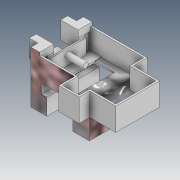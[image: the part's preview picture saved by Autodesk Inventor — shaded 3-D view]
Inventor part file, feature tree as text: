
AUTODESK INVENTOR PART (.ipt)
format: ipt  version: 2021 (Build 250183000, 183)  size: 703,488 bytes
history: native  units: in
note: dims shown in document units (in); Inventor stores cm internally (conversion verified against a paired STEP export)
features: extrude x36, sketch x36, other x1
ambient origin geometry x8: Origin, YZ Plane, XZ Plane, XY Plane, X Axis, Y Axis, Z Axis, Center Point
bodies: Body1 (feature_tree), Body2 (feature_tree)
feature tree (73):
  other  "Sólido1"
  extrude  "Extrusão1"  Depth=0.1969in
  extrude  "Extrusão2"  Depth=0.3937in
  extrude  "Extrusão3"  Depth=0.0984in
  extrude  "Extrusão4"  Depth=0.1969in
  extrude  "Extrusão5"  Depth=0.3937in
  extrude  "Extrusão6"  Depth=0.0079in
  extrude  "Extrusão7"  Depth=0.0079in
  extrude  "Extrusão10"  Depth=0.0079in
  extrude  "Extrusão11"  Depth=0.0079in
  extrude  "Extrusão12"  Depth=0.0079in
  extrude  "Extrusão13"  Depth=0.0079in
  extrude  "Extrusão16"  Depth=0.0079in
  extrude  "Extrusão20"  Depth=0.0079in
  extrude  "Extrusão25"  Depth=0.1575in
  extrude  "Extrusão26"  Depth=0.0079in
  extrude  "Extrusão27"  Depth=0.0394in
  extrude  "Extrusão28"  Depth=0.0787in
  extrude  "Extrusão29"  Depth=1.1811in TaperAngle=0.0deg
  extrude  "Extrusão30"  Depth=0.3543in
  extrude  "Extrusão31"  Depth=0.1181in
  extrude  "Extrusão32"  Depth=0.1969in TaperAngle=0.0deg
  extrude  "Extrusão33"  Depth=0.0591in
  extrude  "Extrusão34"  Depth=0.2559in
  extrude  "Extrusão35"  Depth=0.0315in TaperAngle=0.0deg
  extrude  "Extrusão36"  Depth=0.0394in
  extrude  "Extrusão37"  Depth=0.0394in
  extrude  "Extrusão38"  Depth=0.0394in
  extrude  "Extrusão39"  Depth=0.0394in
  extrude  "Extrusão40"  Depth=0.0394in TaperAngle=0.0deg
  extrude  "Extrusão41"  Depth=0.0197in TaperAngle=0.0deg
  extrude  "Extrusão42"  Depth=0.0197in TaperAngle=0.0deg
  extrude  "Extrusão43"  Depth=0.1969in
  extrude  "Extrusão44"  Depth=0.1181in
  extrude  "Extrusão45"  Depth=0.1969in
  extrude  "Extrusão46"  Depth=0.1181in
  extrude  "Extrusão47"  Depth=0.0039in
  sketch  "Esboço2"  dims[d0=0.1969in d1=0.1969in]
  sketch  "Esboço4"  dims[d2=0.1181in d3=0.3937in]
  sketch  "Esboço5"  dims[d4=0.1969in d5=0.0984in]
  sketch  "Esboço6"  dims[d6=0.3937in d7=0.1969in]
  sketch  "Esboço7"  dims[d8=0.1969in d9=0.3937in]
  sketch  "Esboço8"  dims[d11=0.1969in d12=0.0079in]
  sketch  "Esboço10"  dims[d13=0.0079in d14=0.0079in]
  sketch  "Esboço15"  dims[d15=0.0079in d16=0.0079in]
  sketch  "Esboço16"  dims[d17=0.0079in d19=0.0079in]
  sketch  "Esboço18"  dims[d20=0.0079in d21=0.0079in]
  sketch  "Esboço20"  dims[d22=0.0079in d23=0.0079in]
  sketch  "Esboço23"  dims[d24=0.0079in d25=0.0079in]
  sketch  "Esboço29"  dims[d26=0.0079in d27=0.0079in]
  sketch  "Esboço38"  dims[d28=0.2756in d29=0.1575in]
  sketch  "Esboço39"  dims[d30=0.2756in d31=0.0079in]
  sketch  "Esboço40"  dims[d32=0.0787in d33=0.0394in]
  sketch  "Esboço41"  dims[d34=0.0079in d35=0.0787in]
  sketch  "Esboço42"  dims[d36=0.0394in d37=1.1811in d38=0.0in]
  sketch  "Esboço43"  dims[d39=0.4724in d40=0.3543in]
  sketch  "Esboço44"  dims[d46=0.1969in d47=0.0in d48=0.1181in]
  sketch  "Esboço45"  dims[d49=0.5394in d50=0.0in d51=0.1969in d52=0.0in]
  sketch  "Esboço46"  dims[d53=0.1969in d54=0.0in d55=0.0591in]
  sketch  "Esboço47"  dims[d56=0.1969in d57=0.0in d58=0.2559in]
  sketch  "Esboço48"  dims[d59=0.2559in d60=0.0315in d61=0.0in]
  sketch  "Esboço50"  dims[d68=0.1181in d69=0.0in d70=0.0394in]
  sketch  "Esboço51"  dims[d71=0.0394in d73=0.0394in]
  sketch  "Esboço52"  dims[d74=0.3937in d75=0.0in d76=0.0394in]
  sketch  "Esboço53"  dims[d77=0.0in d78=0.0in d79=0.0394in]
  sketch  "Esboço56"  dims[d80=0.0394in d81=0.0394in d82=0.0in]
  sketch  "Esboço57"  dims[d91=0.4134in d92=0.0197in d93=0.0in]
  sketch  "Esboço58"  dims[d102=0.1181in d103=0.0197in d104=0.0in]
  sketch  "Esboço59"  dims[d128=0.7874in d129=0.1969in]
  sketch  "Esboço61"  dims[d130=0.1969in d131=0.1181in]
  sketch  "Esboço62"  dims[d132=0.3937in d133=0.1969in]
  sketch  "Esboço63"  dims[d134=0.1181in d135=0.1181in]
  sketch  "Esboço64"  dims[d136=0.1969in d137=0.0in d138=0.0039in d139=0.0433in d140=0.0039in d141=0.3858in d142=0.0in d143=0.3937in d144=0.0in d147=0.3858in d148=0.0in d149=0.2283in d150=0.2283in d151=0.0591in d152=0.0in d153=0.0591in d154=0.0in d155=0.1969in d156=0.0in d157=0.3937in d158=0.1969in d159=0.0in d160=0.1969in d161=0.0in d163=0.1575in d164=0.1969in d165=0.0in d166=0.1969in d167=0.0in d170=0.374in d171=0.0in d172=0.7874in d173=0.0472in d174=0.0in d175=0.4134in d176=0.4134in d177=0.8268in d178=0.3937in d179=0.0in d180=0.0197in d181=0.0in d185=0.3465in d186=0.0in d187=0.1181in d188=0.1181in d189=0.4803in d190=0.0in d191=0.4685in d192=0.0in d193=0.0394in d194=0.0394in d195=0.0in d196=0.0709in d197=0.0in d198=1.2402in d199=0.3134in d200=0.0394in d201=0.3528in d202=0.5866in d203=0.5866in d204=0.9843in d205=0.9055in d206=0.5866in d207=0.5866in d208=0.2362in d209=0.2362in d210=0.4567in d211=0.378in d212=0.3921in d213=0.3528in d214=0.3465in d215=0.0in d216=0.0394in d217=0.0394in d218=0.126in d219=0.0in d220=0.0394in d221=0.0in d94=0.0197in d95=0.0344in d96=0.0197in d97=0.0344in d123=0.0197in d124=0.0344in d125=0.0197in d126=0.0344in d168=0.0197in d169=0.0344in d222=0.0197in d223=0.0344in]
